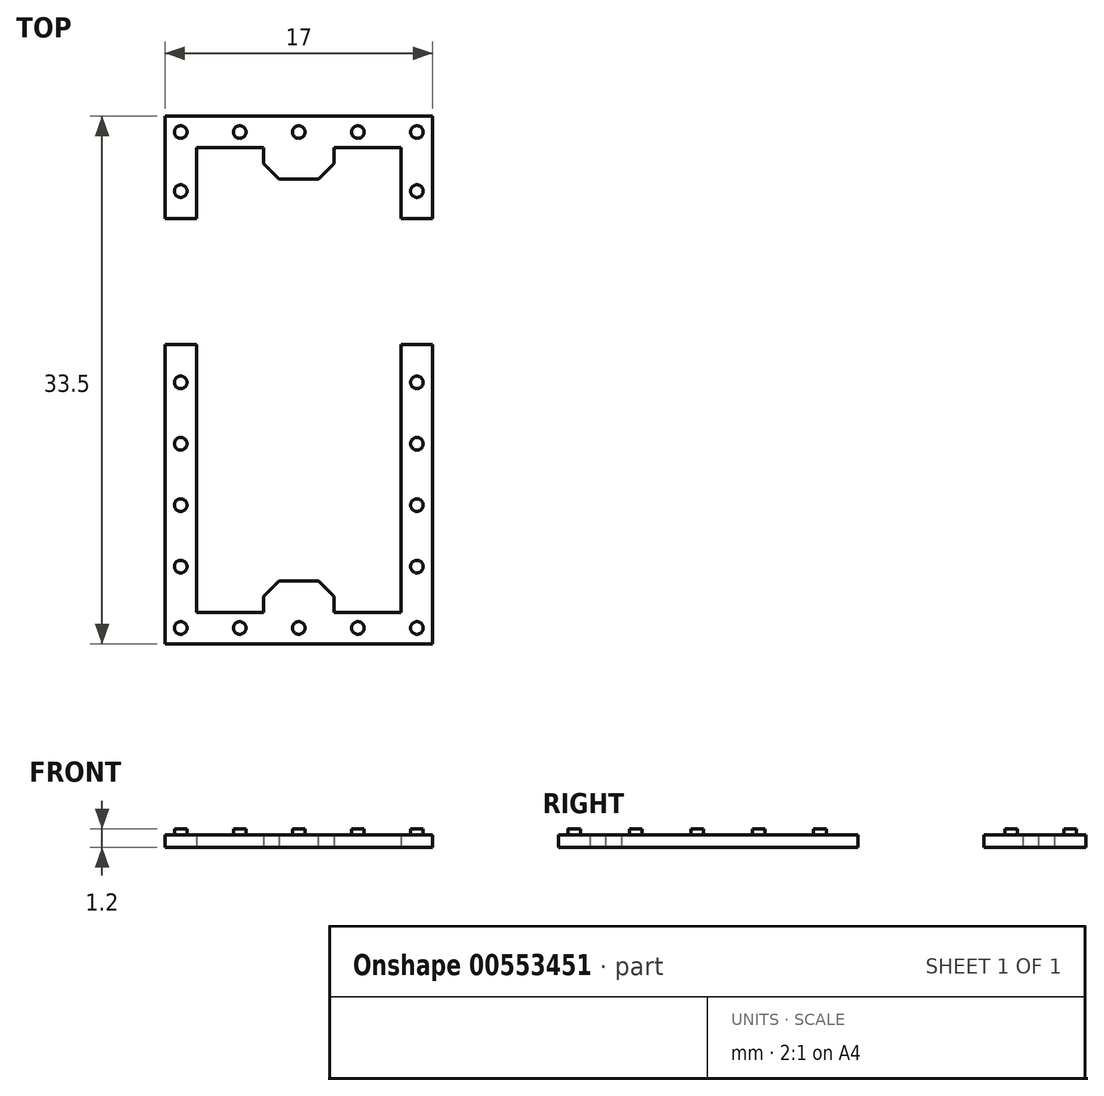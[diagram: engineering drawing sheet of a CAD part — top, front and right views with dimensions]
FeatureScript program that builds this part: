
annotation { "Feature Type Name" : "Feature", "Feature Type Description" : "" }
export const myFeature = defineFeature(function(context is Context, id is Id, definition is map)
    precondition{}
    {
        {
            var Q0;
            Q0=qCreatedBy(makeId("Top.planeOp"),FACE);
            var sketch = newSketch(context, id + "F0", { "sketchPlane" : qUnion([Q0])});
            skLineSegment(sketch, "E0.bottom", {"start": v(-8.5, 10.5) * mm, "end": v(8.5, 10.5) * mm});
            skLineSegment(sketch, "E0.top", {"start": v(-8.5, -23) * mm, "end": v(8.5, -23) * mm});
            skLineSegment(sketch, "E0.left", {"start": v(-8.5, 10.5) * mm, "end": v(-8.5, 4) * mm});
            skLineSegment(sketch, "E0.right", {"start": v(8.5, 10.5) * mm, "end": v(8.5, 4) * mm});
            skLineSegment(sketch, "E1.bottom", {"start": v(-6.5, 8.5) * mm, "end": v(-2.25, 8.5) * mm});
            skLineSegment(sketch, "E1.top", {"start": v(-6.5, -21) * mm, "end": v(-2.25, -21) * mm});
            skLineSegment(sketch, "E1.left", {"start": v(-6.5, 8.5) * mm, "end": v(-6.5, 4) * mm});
            skLineSegment(sketch, "E1.right", {"start": v(6.5, 8.5) * mm, "end": v(6.5, 4) * mm});
            skLineSegment(sketch, "E2", {"start": v(-8.5, 4) * mm, "end": v(-6.5, 4) * mm});
            skLineSegment(sketch, "E3", {"start": v(-8.5, -4) * mm, "end": v(-6.5, -4) * mm});
            skLineSegment(sketch, "E4.trimOffspring", {"start": v(-6.5, -4) * mm, "end": v(-6.5, -21) * mm});
            skLineSegment(sketch, "E5.trimOffspring", {"start": v(-8.5, -4) * mm, "end": v(-8.5, -23) * mm});
            skLineSegment(sketch, "E6.trimOffspring", {"start": v(6.5, -4) * mm, "end": v(6.5, -21) * mm});
            skLineSegment(sketch, "E7.trimOffspring", {"start": v(8.5, -4) * mm, "end": v(8.5, -23) * mm});
            skLineSegment(sketch, "E8.trimOffspring", {"start": v(6.5, 4) * mm, "end": v(8.5, 4) * mm});
            skLineSegment(sketch, "E9.trimOffspring", {"start": v(6.5, -4) * mm, "end": v(8.5, -4) * mm});
            skLineSegment(sketch, "E10.top", {"start": v(-2.25, -19) * mm, "end": v(2.25, -19) * mm});
            skLineSegment(sketch, "E10.left", {"start": v(-2.25, -21) * mm, "end": v(-2.25, -19) * mm});
            skLineSegment(sketch, "E10.right", {"start": v(2.25, -21) * mm, "end": v(2.25, -19) * mm});
            skLineSegment(sketch, "E11.trimOffspring", {"start": v(2.25, -21) * mm, "end": v(6.5, -21) * mm});
            skLineSegment(sketch, "E12", {"start": v(-2.25, 8.5) * mm, "end": v(-2.25, 6.5) * mm});
            skLineSegment(sketch, "E13", {"start": v(-2.25, 6.5) * mm, "end": v(2.25, 6.5) * mm});
            skLineSegment(sketch, "E14", {"start": v(2.25, 6.5) * mm, "end": v(2.25, 8.5) * mm});
            skLineSegment(sketch, "E15.trimOffspring", {"start": v(2.25, 8.5) * mm, "end": v(6.5, 8.5) * mm});
            skSolve(sketch);
        }
        {
            var Q0;
            Q0 = qSketchRegion(id + "F0", true);
            extrude(context, id + "F1", {"entities" : qUnion([Q0]), "depth" : 0.8 * mm, "offsetDistance" : 25 * mm});
        }
        {
            var Q0;
            Q0=makeQuery(id+"F1.opExtrude","CAP_FACE",FACE,{"disambiguationData":[OSD([sQuery(id+"F0.wireOp",EDGE,"E0.bottom"),sQuery(id+"F0.wireOp",EDGE,"E0.left"),sQuery(id+"F0.wireOp",EDGE,"E0.right"),sQuery(id+"F0.wireOp",EDGE,"E1.bottom"),sQuery(id+"F0.wireOp",EDGE,"E1.left"),sQuery(id+"F0.wireOp",EDGE,"E1.right"),sQuery(id+"F0.wireOp",EDGE,"E2"),sQuery(id+"F0.wireOp",EDGE,"E8.trimOffspring")])],"isStart":false});
            var sketch = newSketch(context, id + "F2", { "sketchPlane" : qUnion([Q0])});
            skCircle(sketch, "E16", {"center": v(-7.5, 9.5) * mm, "radius": 0.4 * mm});
            skLineSegment(sketch, "E17.bottom", {"start": v(-7.5, -22) * mm, "end": v(7.5, -22) * mm, "construction": true});
            skLineSegment(sketch, "E17.top", {"start": v(-7.5, 9.5) * mm, "end": v(7.5, 9.5) * mm, "construction": true});
            skLineSegment(sketch, "E17.left", {"start": v(-7.5, -22) * mm, "end": v(-7.5, 9.5) * mm, "construction": true});
            skLineSegment(sketch, "E17.right", {"start": v(7.5, -22) * mm, "end": v(7.5, 9.5) * mm, "construction": true});
            skCircle(sketch, "E18", {"center": v(-3.75, 9.5) * mm, "radius": 0.4 * mm});
            skCircle(sketch, "E19", {"center": v(0, 9.5) * mm, "radius": 0.4 * mm});
            skCircle(sketch, "E20", {"center": v(3.75, 9.5) * mm, "radius": 0.4 * mm});
            skCircle(sketch, "E21", {"center": v(7.5, 9.5) * mm, "radius": 0.4 * mm});
            skCircle(sketch, "E22", {"center": v(-7.5, 5.75) * mm, "radius": 0.4 * mm});
            skCircle(sketch, "E23", {"center": v(7.5, 5.75) * mm, "radius": 0.4 * mm});
            skCircle(sketch, "E24", {"center": v(0, -22) * mm, "radius": 0.4 * mm});
            skCircle(sketch, "E25", {"center": v(3.75, -22) * mm, "radius": 0.4 * mm});
            skCircle(sketch, "E26", {"center": v(7.5, -22) * mm, "radius": 0.4 * mm});
            skCircle(sketch, "E27", {"center": v(-3.75, -22) * mm, "radius": 0.4 * mm});
            skCircle(sketch, "E28", {"center": v(-7.5, -22) * mm, "radius": 0.4 * mm});
            skCircle(sketch, "E29", {"center": v(-7.5, -18.1) * mm, "radius": 0.4 * mm});
            skCircle(sketch, "E30", {"center": v(-7.5, -14.2) * mm, "radius": 0.4 * mm});
            skCircle(sketch, "E31", {"center": v(-7.5, -10.3) * mm, "radius": 0.4 * mm});
            skCircle(sketch, "E32", {"center": v(-7.5, -6.4) * mm, "radius": 0.4 * mm});
            skCircle(sketch, "E33", {"center": v(7.5, -18.1) * mm, "radius": 0.4 * mm});
            skCircle(sketch, "E34", {"center": v(7.5, -14.2) * mm, "radius": 0.4 * mm});
            skCircle(sketch, "E35", {"center": v(7.5, -10.3) * mm, "radius": 0.4 * mm});
            skCircle(sketch, "E36", {"center": v(7.5, -6.4) * mm, "radius": 0.4 * mm});
            skSolve(sketch);
        }
        {
            var Q0;
            Q0 = qSketchRegion(id + "F2", true);
            extrude(context, id + "F3", {"entities" : qUnion([Q0]), "depth" : 0.4 * mm, "offsetDistance" : 25 * mm});
        }
        {
            var Q0;
            Q0=makeQuery(id+"F1.opExtrude","SWEPT_EDGE",EDGE,{"disambiguationData":[OSD([sQuery(id+"F0.wireOp",EDGE,"E12"),sQuery(id+"F0.wireOp",EDGE,"E13")])]});
            var Q1;
            Q1=makeQuery(id+"F1.opExtrude","SWEPT_EDGE",EDGE,{"disambiguationData":[OSD([sQuery(id+"F0.wireOp",EDGE,"E13"),sQuery(id+"F0.wireOp",EDGE,"E14")])]});
            var Q2;
            Q2=makeQuery(id+"F1.opExtrude","SWEPT_EDGE",EDGE,{"disambiguationData":[OSD([sQuery(id+"F0.wireOp",EDGE,"E10.top"),sQuery(id+"F0.wireOp",EDGE,"E10.right")])]});
            var Q3;
            Q3=makeQuery(id+"F1.opExtrude","SWEPT_EDGE",EDGE,{"disambiguationData":[OSD([sQuery(id+"F0.wireOp",EDGE,"E10.top"),sQuery(id+"F0.wireOp",EDGE,"E10.left")])]});
            chamfer(context, id + "F4", {"entities" : qUnion([Q0, Q1, Q2, Q3]), "width" : 1 * mm, "tangentPropagation" : true});
        }
    });
